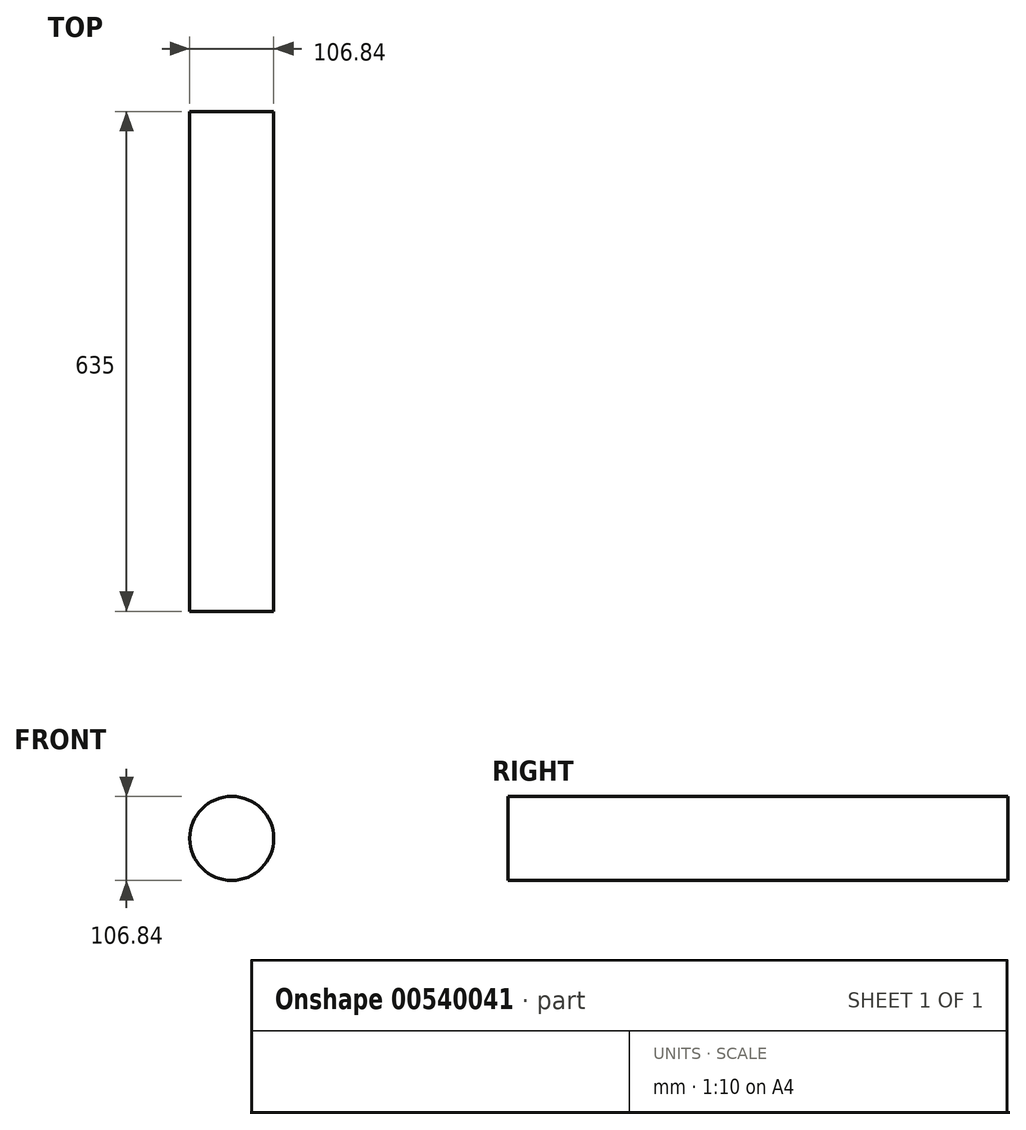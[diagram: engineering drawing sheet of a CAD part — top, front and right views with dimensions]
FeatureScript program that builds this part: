
annotation { "Feature Type Name" : "Feature", "Feature Type Description" : "" }
export const myFeature = defineFeature(function(context is Context, id is Id, definition is map)
    precondition{}
    {
        {
            var Q0;
            Q0=qCreatedBy(makeId("Front.planeOp"),FACE);
            var sketch = newSketch(context, id + "F0", { "sketchPlane" : qUnion([Q0])});
            skCircle(sketch, "E0", {"center": v(0, 0) * mm, "radius": 53.42 * mm});
            skSolve(sketch);
        }
        {
            var Q0;
            Q0 = qSketchRegion(id + "F0", true);
            extrude(context, id + "F1", {"entities" : qUnion([Q0]), "depth" : 635 * mm, "offsetDistance" : 25.4 * mm});
        }
    });
